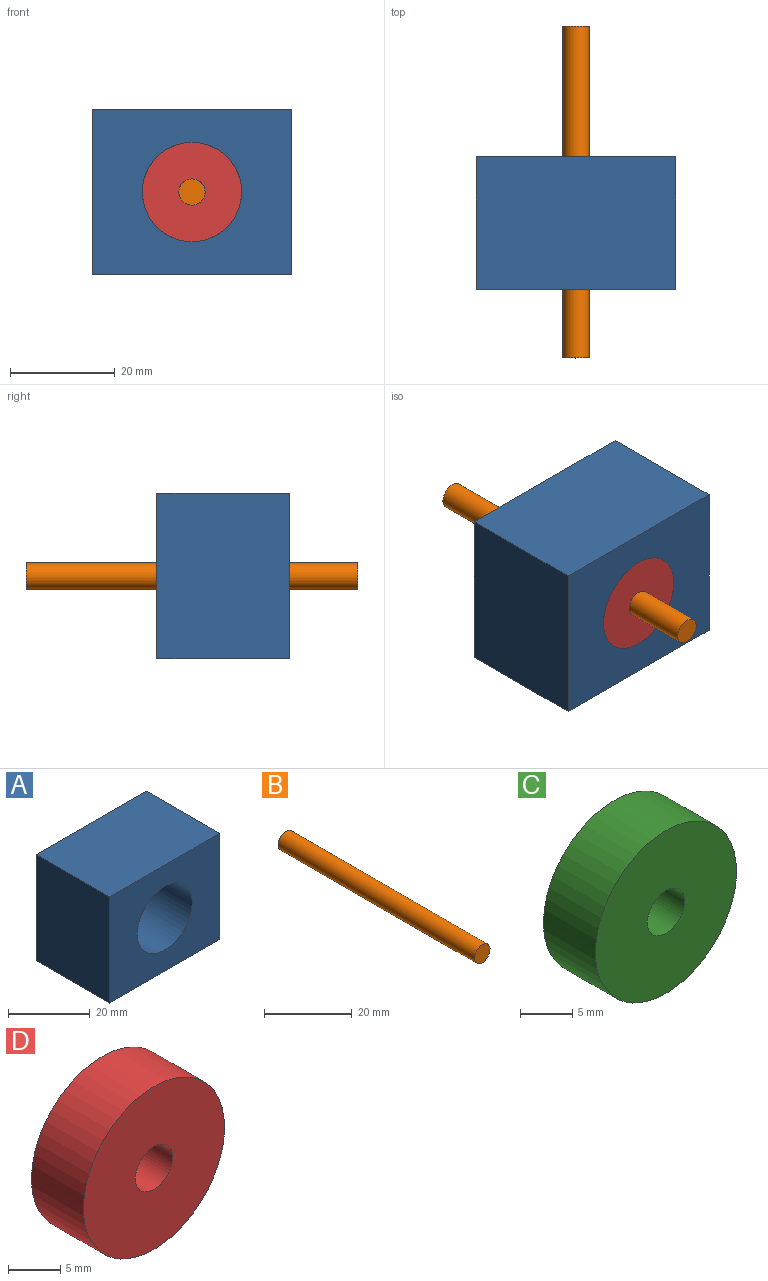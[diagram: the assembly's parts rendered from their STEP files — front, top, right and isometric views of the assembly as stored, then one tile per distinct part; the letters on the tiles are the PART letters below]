
ASSEMBLY  parts=4 mates=3
PART A: 11 faces, bbox 38.1x25.4x31.8 mm
  f0: plane 31.75x25.4mm, normal (-1,0,0), area 806.5mm2, adj f1,f3,f4,f5
  f1: plane 38.1x25.4mm, normal (0,0,-1), area 949mm2, adj f0,f2,f4,f5,f8,f10
  f2: plane 31.75x25.4mm, normal (1,0,0), area 806.5mm2, adj f1,f3,f4,f5
  f3: plane 38.1x25.4mm, normal (0,0,1), area 967.7mm2, adj f0,f2,f4,f5
  f4: plane 38.1x31.75mm, normal (0,-1,0), area 926.1mm2, adj f0,f1,f2,f3,f6
  f5: plane 38.1x31.75mm, normal (0,1,0), area 926.1mm2, adj f0,f1,f2,f3,f6
  f6: cylinder r=9.5mm len=25.4mm, axis (0,1,0), area 1516.1mm2, adj f4,f5
  f7: cone r=0mm half-angle=59deg, axis (0,0,-1), area 10.9mm2, adj f8
  f8: cylinder r=1.73mm len=15.08mm, axis (0,0,-1), area 163.7mm2, adj f1,f7
  f9: cone r=0mm half-angle=59deg, axis (0,0,-1), area 10.9mm2, adj f10
  f10: cylinder r=1.73mm len=15.08mm, axis (0,0,-1), area 163.7mm2, adj f1,f9
PART B: 3 faces, bbox 5x63.5x5 mm
  f0: cylinder r=2.5mm len=63.5mm, axis (0,1,0), area 997.5mm2, adj f1,f2
  f1: plane 5x5mm, normal (0,-1,0), area 19.6mm2, adj f0
  f2: plane 5x5mm, normal (0,1,0), area 19.6mm2, adj f0
PART C: 4 faces, bbox 19x7x19 mm
  f0: cylinder r=2.5mm len=7mm, axis (0,1,0), area 110mm2, adj f2,f3
  f1: cylinder r=9.5mm len=19mm, axis (0,1,0), area 417.8mm2, adj f2,f3
  f2: plane 19x19mm, normal (0,-1,0), area 263.9mm2, adj f0,f1
  f3: plane 19x19mm, normal (0,1,0), area 263.9mm2, adj f0,f1
PART D: 4 faces, bbox 19x7x19 mm
  f0: cylinder r=2.5mm len=7mm, axis (0,-1,0), area 110mm2, adj f2,f3
  f1: cylinder r=9.5mm len=19mm, axis (0,-1,0), area 417.8mm2, adj f2,f3
  f2: plane 19x19mm, normal (0,1,0), area 263.9mm2, adj f0,f1
  f3: plane 19x19mm, normal (0,-1,0), area 263.9mm2, adj f0,f1
PLACE A t=(0,12.7,0)mm
PLACE B rot(axis=(0,-1,0),4.6deg) t=(0,37.73,0)mm
PLACE C t=(0,12.7,0)mm
PLACE D t=(0,12.7,0)mm
MATE fastened C.f1 <-> A.f6  axis (0,1,0) through (0,12.7,0)mm
MATE fastened D.f1 <-> A.f6  axis (0,-1,0) through (0,-12.7,0)mm
MATE cylindrical B.f0 <-> D.f0  axis (0,1,0) through (0,5.98,0)mm
